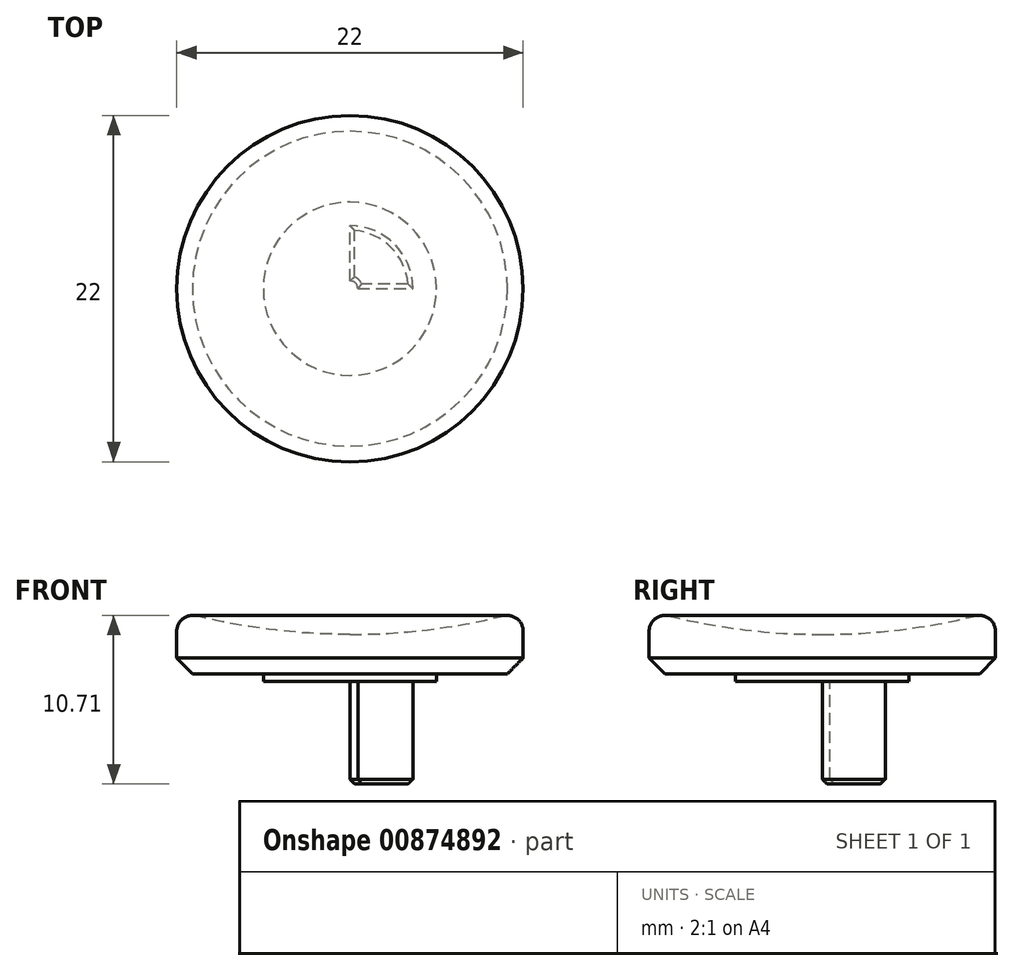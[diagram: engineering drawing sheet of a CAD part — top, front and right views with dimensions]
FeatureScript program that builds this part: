
annotation { "Feature Type Name" : "Feature", "Feature Type Description" : "" }
export const myFeature = defineFeature(function(context is Context, id is Id, definition is map)
    precondition{}
    {
        {
            var Q0;
            Q0=qCreatedBy(makeId("Front.planeOp"),FACE);
            var sketch = newSketch(context, id + "F0", { "sketchPlane" : qUnion([Q0])});
            skArc(sketch, "E0", {"start": v(0, 2.5) * mm, "mid": v(5.55, 2.88) * mm, "end": v(11, 4) * mm});
            skLineSegment(sketch, "E1", {"start": v(0, 2.5) * mm, "end": v(0, 0) * mm});
            skLineSegment(sketch, "E2", {"start": v(0, 0) * mm, "end": v(11, 0) * mm});
            skLineSegment(sketch, "E3", {"start": v(11, 0) * mm, "end": v(11, 4) * mm});
            skLineSegment(sketch, "E4", {"start": v(0, 2.5) * mm, "end": v(-3.82, 2.5) * mm, "construction": true});
            skLineSegment(sketch, "E5", {"start": v(0, 0) * mm, "end": v(0, -0.5) * mm});
            skLineSegment(sketch, "E6", {"start": v(0, -0.5) * mm, "end": v(5.5, -0.5) * mm});
            skLineSegment(sketch, "E7", {"start": v(5.5, -0.5) * mm, "end": v(5.5, 0) * mm});
            skSolve(sketch);
        }
        {
            var Q0;
            Q0=makeQuery(id+"F0.imprint","IMPRINT",FACE,{"disambiguationData":[TD([[makeQuery(id+"F0.imprint","IMPRINT",EDGE,{"derivedFrom":sQuery(id+"F0.wireOp",EDGE,"E0")}),-1.0]])]});
            var Q1;
            {var subQ0=sQuery(id+"F0.wireOp",EDGE,"E5");Q1=makeQuery(id+"F0.imprint","IMPRINT",FACE,{"disambiguationData":[TD([[makeQuery(id+"F0.imprint","IMPRINT",EDGE,{"derivedFrom":subQ0}),1.0]])]});}
            var Q2;
            Q2=sQuery(id+"F0.wireOp",EDGE,"E1");
            revolve(context, id + "F1", {"surfaceOperationType" : NewSurfaceOperationType.NEW, "entities" : qUnion([Q0, Q1]), "axis" : qUnion([Q2]), "revolveType" : RevolveType.FULL});
        }
        {
            var Q0;
            Q0=makeQuery(id+"F1.opRevolve","SWEPT_EDGE",EDGE,{"disambiguationData":[OSD([sQuery(id+"F0.wireOp",EDGE,"E2"),sQuery(id+"F0.wireOp",EDGE,"E3")])]});
            chamfer(context, id + "F2", {"entities" : qUnion([Q0]), "width" : 1 * mm, "tangentPropagation" : true});
        }
        {
            var Q0;
            Q0=makeQuery(id+"F1.opRevolve","SWEPT_EDGE",EDGE,{"disambiguationData":[OSD([sQuery(id+"F0.wireOp",EDGE,"E0"),sQuery(id+"F0.wireOp",EDGE,"E3")])]});
            fillet(context, id + "F3", {"entities" : qUnion([Q0]), "radius" : 1 * mm, "tangentPropagation" : true, "allowEdgeOverflow" : false});
        }
        {
            var Q0;
            Q0=makeQuery(id+"F1.opRevolve","SWEPT_FACE",FACE,{"disambiguationData":[OSD([sQuery(id+"F0.wireOp",EDGE,"E6")])]});
            var sketch = newSketch(context, id + "F4", { "sketchPlane" : qUnion([Q0])});
            skCircle(sketch, "E8", {"center": v(0, 0) * mm, "radius": 0.5 * mm});
            skCircle(sketch, "E9", {"center": v(0, 0) * mm, "radius": 4 * mm});
            skLineSegment(sketch, "E10", {"start": v(0, 4) * mm, "end": v(0, -4) * mm});
            skLineSegment(sketch, "E11", {"start": v(-4, 0) * mm, "end": v(4, 0) * mm});
            skSolve(sketch);
        }
        {
            var Q0;
            {var subQ0=sQuery(id+"F4.wireOp",EDGE,"E10");var subQ1=sQuery(id+"F4.wireOp",EDGE,"E8");var subQ2=makeQuery(id+"F4.imprint","INTERSECT",VERTEX,{"disambiguationData":[OD(0.0)],"derivedFrom":[subQ1,subQ0]});Q0=makeQuery(id+"F4.imprint","IMPRINT",FACE,{"disambiguationData":[TD([[makeQuery(id+"F4.imprint","IMPRINT",EDGE,{"disambiguationData":[TD([[subQ2,-1.0]])],"derivedFrom":subQ1}),-1.0]])]});}
            var Q1;
            {var subQ0=sQuery(id+"F4.wireOp",EDGE,"E11");var subQ1=sQuery(id+"F4.wireOp",EDGE,"E8");var subQ2=makeQuery(id+"F4.imprint","INTERSECT",VERTEX,{"disambiguationData":[OD(0.0)],"derivedFrom":[subQ1,subQ0]});Q1=makeQuery(id+"F4.imprint","IMPRINT",FACE,{"disambiguationData":[TD([[makeQuery(id+"F4.imprint","IMPRINT",EDGE,{"disambiguationData":[TD([[subQ2,1.0]])],"derivedFrom":subQ1}),-1.0]])]});}
            extrude(context, id + "F5", {"entities" : qUnion([Q0, Q1]), "operationType" : NewBodyOperationType.ADD, "depth" : 6.5 * mm, "offsetDistance" : 25 * mm});
        }
        {
            var Q0;
            {var subQ0=sQuery(id+"F4.wireOp",EDGE,"E11");var subQ1=sQuery(id+"F4.wireOp",EDGE,"E9");var subQ2=makeQuery(id+"F4.imprint","INTERSECT",VERTEX,{"disambiguationData":[OD(1.0)],"derivedFrom":[subQ1,subQ0]});var subQ3=sQuery(id+"F4.wireOp",EDGE,"E8");var subQ4=makeQuery(id+"F4.imprint","INTERSECT",VERTEX,{"disambiguationData":[OD(0.0)],"derivedFrom":[subQ3,subQ0]});var subQ5=sQuery(id+"F4.wireOp",EDGE,"E10");var subQ6=makeQuery(id+"F4.imprint","INTERSECT",VERTEX,{"disambiguationData":[OD(1.0)],"derivedFrom":[subQ1,subQ5]});Q0=makeQuery(id+"F5.opExtrude","CAP_FACE",FACE,{"disambiguationData":[OSD([subQ3,subQ1,subQ5,subQ0]),TDD([makeQuery(id+"F4.imprint","IMPRINT",EDGE,{"disambiguationData":[TD([[subQ4,1.0]])],"derivedFrom":subQ3}),makeQuery(id+"F4.imprint","IMPRINT",EDGE,{"disambiguationData":[TD([[subQ6,-1.0]])],"derivedFrom":subQ1}),makeQuery(id+"F4.imprint","IMPRINT",EDGE,{"disambiguationData":[TD([[subQ6,1.0]])],"derivedFrom":subQ5}),makeQuery(id+"F4.imprint","IMPRINT",EDGE,{"disambiguationData":[TD([[subQ2,1.0]])],"derivedFrom":subQ0})])],"isStart":false});}
            var Q1;
            {var subQ0=sQuery(id+"F4.wireOp",EDGE,"E11");var subQ1=sQuery(id+"F4.wireOp",EDGE,"E9");var subQ2=makeQuery(id+"F4.imprint","INTERSECT",VERTEX,{"disambiguationData":[OD(0.0)],"derivedFrom":[subQ1,subQ0]});var subQ3=sQuery(id+"F4.wireOp",EDGE,"E8");var subQ5=sQuery(id+"F4.wireOp",EDGE,"E10");var subQ6=makeQuery(id+"F4.imprint","INTERSECT",VERTEX,{"disambiguationData":[OD(0.0)],"derivedFrom":[subQ1,subQ5]});var subQ7=makeQuery(id+"F4.imprint","INTERSECT",VERTEX,{"disambiguationData":[OD(0.0)],"derivedFrom":[subQ3,subQ5]});Q1=makeQuery(id+"F5.opExtrude","CAP_FACE",FACE,{"disambiguationData":[OSD([subQ3,subQ1,subQ5,subQ0]),TDD([makeQuery(id+"F4.imprint","IMPRINT",EDGE,{"disambiguationData":[TD([[subQ7,-1.0]])],"derivedFrom":subQ3}),makeQuery(id+"F4.imprint","IMPRINT",EDGE,{"disambiguationData":[TD([[subQ6,-1.0]])],"derivedFrom":subQ1}),makeQuery(id+"F4.imprint","IMPRINT",EDGE,{"disambiguationData":[TD([[subQ6,-1.0]])],"derivedFrom":subQ5}),makeQuery(id+"F4.imprint","IMPRINT",EDGE,{"disambiguationData":[TD([[subQ2,-1.0]])],"derivedFrom":subQ0})])],"isStart":false});}
            chamfer(context, id + "F6", {"entities" : qUnion([Q0, Q1]), "width" : 0.3 * mm, "tangentPropagation" : true});
        }
    });
